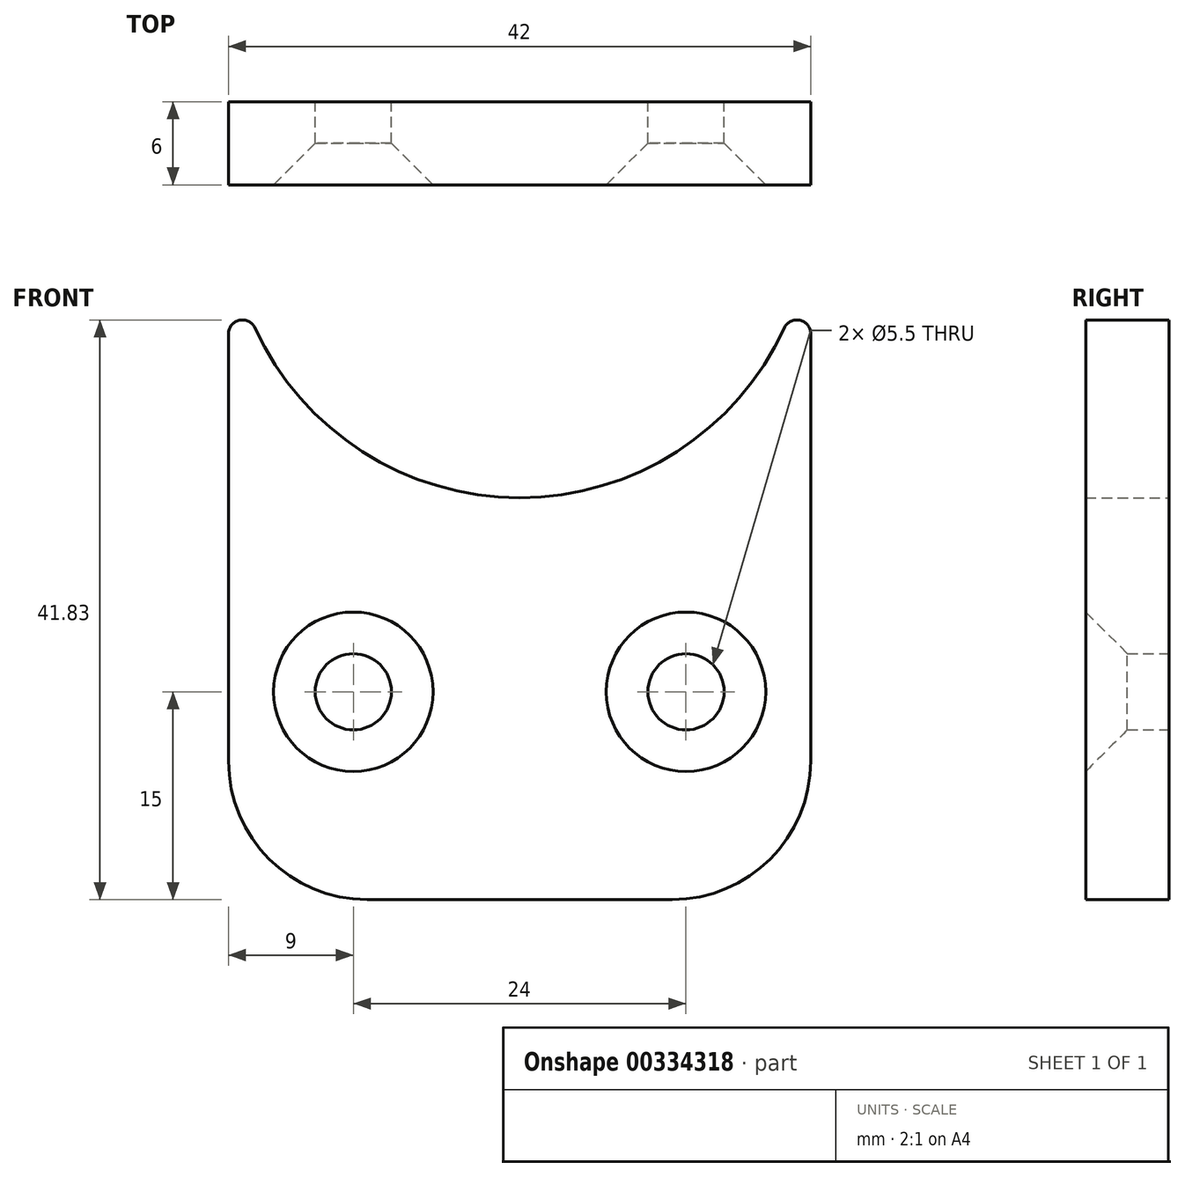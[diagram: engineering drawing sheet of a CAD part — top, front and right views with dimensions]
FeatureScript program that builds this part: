
annotation { "Feature Type Name" : "Feature", "Feature Type Description" : "" }
export const myFeature = defineFeature(function(context is Context, id is Id, definition is map)
    precondition{}
    {
        {
            var Q0;
            Q0=qCreatedBy(makeId("Front.planeOp"),FACE);
            var sketch = newSketch(context, id + "F0", { "sketchPlane" : qUnion([Q0])});
            skCircle(sketch, "E0", {"center": v(0, 0) * mm, "radius": 21 * mm, "construction": true});
            skPoint(sketch, "E1.orphan", {"position": v(-26.43, 0) * mm});
            skArc(sketch, "E2", {"start": v(-21, 0) * mm, "mid": v(0, -21) * mm, "end": v(21, 0) * mm});
            skLineSegment(sketch, "E3", {"start": v(-21, 0) * mm, "end": v(-21, -40) * mm});
            skLineSegment(sketch, "E4", {"start": v(-11, -50) * mm, "end": v(11, -50) * mm});
            skLineSegment(sketch, "E5", {"start": v(21, -40) * mm, "end": v(21, 0) * mm});
            skPoint(sketch, "E6.visualSharp", {"position": v(-21, -50) * mm});
            skArc(sketch, "E6.filletArc", {"start": v(-21, -40) * mm, "mid": v(-18.07, -47.07) * mm, "end": v(-11, -50) * mm});
            skPoint(sketch, "E7.visualSharp", {"position": v(21, -50) * mm});
            skArc(sketch, "E7.filletArc", {"start": v(11, -50) * mm, "mid": v(18.07, -47.07) * mm, "end": v(21, -40) * mm});
            skLineSegment(sketch, "E8", {"start": v(0, 26.57) * mm, "end": v(0, -60.87) * mm, "construction": true});
            skLineSegment(sketch, "E9", {"start": v(-27.2, -35) * mm, "end": v(29.77, -35) * mm, "construction": true});
            skCircle(sketch, "E10", {"center": v(-12, -35) * mm, "radius": 2.75 * mm});
            skCircle(sketch, "E11", {"center": v(12, -35) * mm, "radius": 2.75 * mm});
            skSolve(sketch);
        }
        {
            var Q0;
            Q0=qSketchRegion(id+"F0",true);
            extrude(context, id + "F1", {"entities" : qUnion([Q0]), "depth" : 6 * mm});
        }
        {
            var Q0;
            Q0=makeQuery(id+"F1.opExtrude","SWEPT_EDGE",EDGE,{"disambiguationData":[OSD([sQuery(id+"F0.wireOp",EDGE,"E2"),sQuery(id+"F0.wireOp",EDGE,"E3")])]});
            var Q1;
            Q1=makeQuery(id+"F1.opExtrude","SWEPT_EDGE",EDGE,{"disambiguationData":[OSD([sQuery(id+"F0.wireOp",EDGE,"E2"),sQuery(id+"F0.wireOp",EDGE,"E5")])]});
            fillet(context, id + "F2", {"entities" : qUnion([Q0, Q1]), "radius" : 1 * mm, "tangentPropagation" : true, "allowEdgeOverflow" : false});
        }
        {
            var Q0;
            Q0=makeQuery(id+"F1.opExtrude","CAP_EDGE",EDGE,{"disambiguationData":[OSD([sQuery(id+"F0.wireOp",EDGE,"E10")])],"isStart":false});
            var Q1;
            Q1=makeQuery(id+"F1.opExtrude","CAP_EDGE",EDGE,{"disambiguationData":[OSD([sQuery(id+"F0.wireOp",EDGE,"E11")])],"isStart":false});
            chamfer(context, id + "F3", {"entities" : qUnion([Q0, Q1]), "width" : 3 * mm, "tangentPropagation" : true});
        }
    });
